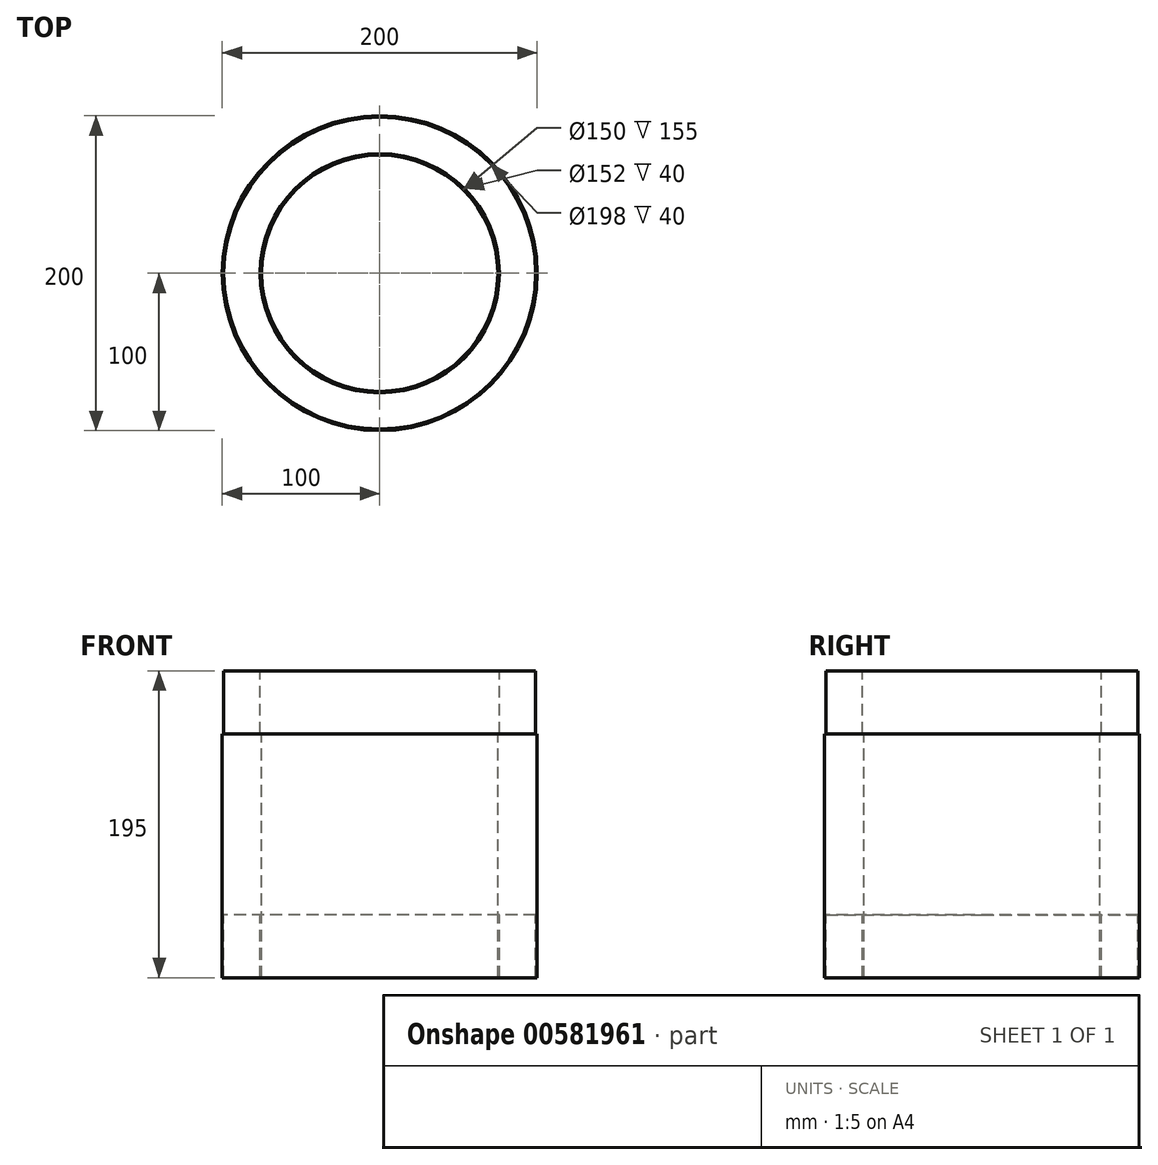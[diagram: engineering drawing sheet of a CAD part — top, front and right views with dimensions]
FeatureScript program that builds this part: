
annotation { "Feature Type Name" : "Feature", "Feature Type Description" : "" }
export const myFeature = defineFeature(function(context is Context, id is Id, definition is map)
    precondition{}
    {
        {
            var Q0;
            Q0=qCreatedBy(makeId("Front.planeOp"),FACE);
            var sketch = newSketch(context, id + "F0", { "sketchPlane" : qUnion([Q0])});
            skLineSegment(sketch, "E0", {"start": v(0, 345.75) * mm, "end": v(0, -558.03) * mm, "construction": true});
            skLineSegment(sketch, "E1", {"start": v(-75, -518.84) * mm, "end": v(-75, -363.84) * mm});
            skLineSegment(sketch, "E2", {"start": v(-75, -363.84) * mm, "end": v(-76, -363.84) * mm});
            skLineSegment(sketch, "E3", {"start": v(-76, -363.84) * mm, "end": v(-76, -323.84) * mm});
            skLineSegment(sketch, "E4", {"start": v(-76, -323.84) * mm, "end": v(-99, -323.84) * mm});
            skLineSegment(sketch, "E5", {"start": v(-99, -323.84) * mm, "end": v(-99, -363.84) * mm});
            skLineSegment(sketch, "E6", {"start": v(-99, -363.84) * mm, "end": v(-100, -363.84) * mm});
            skLineSegment(sketch, "E7", {"start": v(-100, -363.84) * mm, "end": v(-100, -518.84) * mm});
            skLineSegment(sketch, "E8", {"start": v(-100, -518.84) * mm, "end": v(-99, -518.84) * mm});
            skLineSegment(sketch, "E9", {"start": v(-99, -518.84) * mm, "end": v(-99, -478.84) * mm});
            skLineSegment(sketch, "E10", {"start": v(-99, -478.84) * mm, "end": v(-76, -478.84) * mm});
            skLineSegment(sketch, "E11", {"start": v(-76, -478.84) * mm, "end": v(-76, -518.84) * mm});
            skLineSegment(sketch, "E12", {"start": v(-76, -518.84) * mm, "end": v(-75, -518.84) * mm});
            skSolve(sketch);
        }
        {
            var Q0;
            Q0=qSketchRegion(id+"F0",true);
            var Q1;
            Q1=sQuery(id+"F0.wireOp",EDGE,"E0");
            revolve(context, id + "F1", {"entities" : qUnion([Q0]), "axis" : qUnion([Q1]), "revolveType" : RevolveType.FULL});
        }
    });
